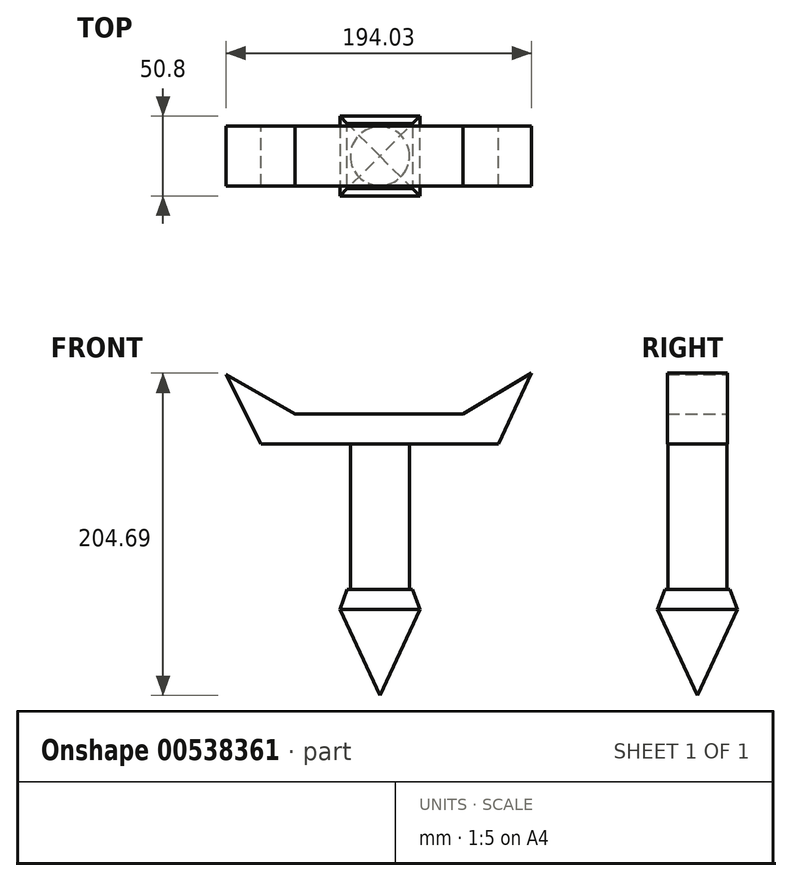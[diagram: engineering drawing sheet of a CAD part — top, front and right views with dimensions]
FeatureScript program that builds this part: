
annotation { "Feature Type Name" : "Feature", "Feature Type Description" : "" }
export const myFeature = defineFeature(function(context is Context, id is Id, definition is map)
    precondition{}
    {
        {
            var Q0;
            Q0=qCreatedBy(makeId("Top.planeOp"),FACE);
            var sketch = newSketch(context, id + "F0", { "sketchPlane" : qUnion([Q0])});
            skLineSegment(sketch, "E0.bottom", {"start": v(25.4, 25.4) * mm, "end": v(-25.4, 25.4) * mm});
            skLineSegment(sketch, "E0.top", {"start": v(25.4, -25.4) * mm, "end": v(-25.4, -25.4) * mm});
            skLineSegment(sketch, "E0.left", {"start": v(25.4, 25.4) * mm, "end": v(25.4, -25.4) * mm});
            skLineSegment(sketch, "E0.right", {"start": v(-25.4, 25.4) * mm, "end": v(-25.4, -25.4) * mm});
            skPoint(sketch, "E0.middle", {"position": v(0, 0) * mm});
            skSolve(sketch);
        }
        {
            var Q0;
            Q0 = qSketchRegion(id + "F0", true);
            extrude(context, id + "F1", {"entities" : qUnion([Q0]), "oppositeDirection" : true, "depth" : 76.2 * mm, "offsetDistance" : 25.4 * mm, "hasDraft" : true, "draftAngle" : 25 * degree, "draftPullDirection" : true});
        }
        {
            var Q0;
            Q0=makeQuery(id+"F1.opExtrude","CAP_FACE",FACE,{"disambiguationData":[OSD([sQuery(id+"F0.wireOp",EDGE,"E0.bottom"),sQuery(id+"F0.wireOp",EDGE,"E0.top"),sQuery(id+"F0.wireOp",EDGE,"E0.left"),sQuery(id+"F0.wireOp",EDGE,"E0.right")])],"isStart":true});
            extrude(context, id + "F2", {"entities" : qUnion([Q0]), "operationType" : NewBodyOperationType.ADD, "depth" : 12.7 * mm, "offsetDistance" : 25.4 * mm, "hasDraft" : true, "draftAngle" : 20 * degree, "draftPullDirection" : true});
        }
        {
            var Q0;
            Q0=makeQuery(id+"F2.opExtrude","CAP_FACE",FACE,{"disambiguationData":[OSD([sQuery(id+"F0.wireOp",EDGE,"E0.bottom"),sQuery(id+"F0.wireOp",EDGE,"E0.top"),sQuery(id+"F0.wireOp",EDGE,"E0.left"),sQuery(id+"F0.wireOp",EDGE,"E0.right")])],"isStart":false});
            var sketch = newSketch(context, id + "F3", { "sketchPlane" : qUnion([Q0])});
            skCircle(sketch, "E1", {"center": v(0, 0) * mm, "radius": 18.77 * mm});
            skSolve(sketch);
        }
        {
            var Q0;
            Q0 = qSketchRegion(id + "F3", true);
            extrude(context, id + "F4", {"entities" : qUnion([Q0]), "operationType" : NewBodyOperationType.ADD, "depth" : 101.6 * mm, "offsetDistance" : 25.4 * mm});
        }
        {
            var Q0;
            Q0=qCreatedBy(makeId("Front.planeOp"),FACE);
            var sketch = newSketch(context, id + "F5", { "sketchPlane" : qUnion([Q0])});
            skLineSegment(sketch, "E2.bottom", {"start": v(52.8, 124.25) * mm, "end": v(-53.85, 124.25) * mm});
            skLineSegment(sketch, "E2.top", {"start": v(75.35, 105.24) * mm, "end": v(-75.35, 105.24) * mm});
            skPoint(sketch, "E2.middle", {"position": v(0, 114.74) * mm});
            skLineSegment(sketch, "E3", {"start": v(-53.85, 124.25) * mm, "end": v(-97.75, 149.51) * mm});
            skLineSegment(sketch, "E4", {"start": v(-97.75, 149.51) * mm, "end": v(-75.35, 105.24) * mm});
            skLineSegment(sketch, "E5", {"start": v(52.8, 124.25) * mm, "end": v(96.28, 150.22) * mm});
            skLineSegment(sketch, "E6", {"start": v(96.28, 150.22) * mm, "end": v(75.35, 105.24) * mm});
            skPoint(sketch, "E2.right.start.orphan", {"position": v(-75.35, 124.25) * mm});
            skPoint(sketch, "E2.left.start.orphan", {"position": v(75.35, 124.25) * mm});
            skSolve(sketch);
        }
        {
            var Q0;
            Q0 = qSketchRegion(id + "F5", true);
            extrude(context, id + "F6", {"entities" : qUnion([Q0]), "operationType" : NewBodyOperationType.ADD, "endBound" : BoundingType.SYMMETRIC, "depth" : 38.1 * mm, "offsetDistance" : 25.4 * mm});
        }
    });
